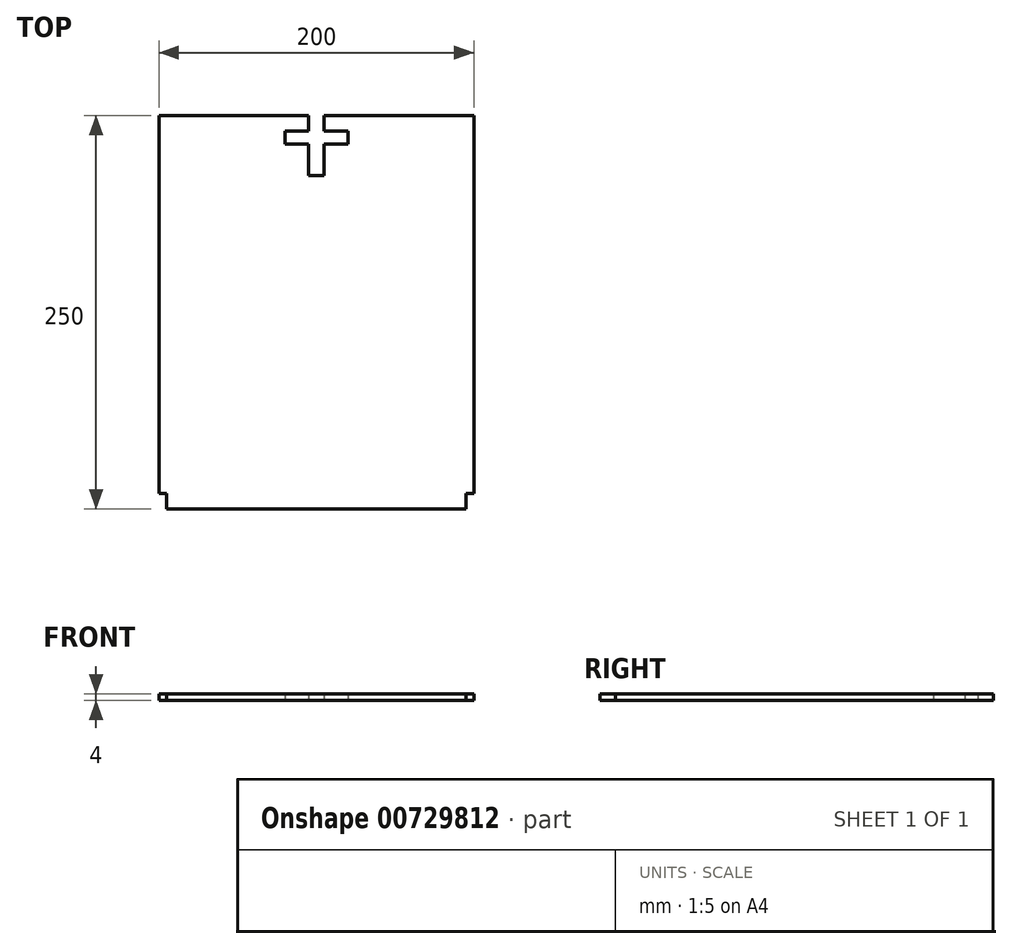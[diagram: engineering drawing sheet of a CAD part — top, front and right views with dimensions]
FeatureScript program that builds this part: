
annotation { "Feature Type Name" : "Feature", "Feature Type Description" : "" }
export const myFeature = defineFeature(function(context is Context, id is Id, definition is map)
    precondition{}
    {
        {
            var Q0;
            Q0=qCreatedBy(makeId("Top.planeOp"),FACE);
            var sketch = newSketch(context, id + "F0", { "sketchPlane" : qUnion([Q0])});
            skLineSegment(sketch, "E0.bottom", {"start": v(20, -10) * mm, "end": v(5, -10) * mm});
            skLineSegment(sketch, "E0.left", {"start": v(20, -10) * mm, "end": v(20, -18) * mm});
            skLineSegment(sketch, "E0.right", {"start": v(-20, -10) * mm, "end": v(-20, -18) * mm});
            skPoint(sketch, "E0.middle", {"position": v(0, 0) * mm});
            skLineSegment(sketch, "E1.top", {"start": v(-100, 0) * mm, "end": v(-5, 0) * mm});
            skLineSegment(sketch, "E1.left", {"start": v(-100, -240) * mm, "end": v(-100, 0) * mm});
            skLineSegment(sketch, "E1.right", {"start": v(100, -240) * mm, "end": v(100, 0) * mm});
            skLineSegment(sketch, "E2", {"start": v(20, -18) * mm, "end": v(5, -18) * mm});
            skLineSegment(sketch, "E3", {"start": v(5, -18) * mm, "end": v(5, -38) * mm});
            skLineSegment(sketch, "E4", {"start": v(-20, -18) * mm, "end": v(-5, -18) * mm});
            skLineSegment(sketch, "E5", {"start": v(-5, -18) * mm, "end": v(-5, -38) * mm});
            skLineSegment(sketch, "E6", {"start": v(0, 0) * mm, "end": v(0, -10) * mm, "construction": true});
            skLineSegment(sketch, "E7", {"start": v(95, -250) * mm, "end": v(-95, -250) * mm});
            skLineSegment(sketch, "E8", {"start": v(0, -38) * mm, "end": v(0, -250) * mm, "construction": true});
            skLineSegment(sketch, "E9", {"start": v(-100, -240) * mm, "end": v(-95, -240) * mm});
            skLineSegment(sketch, "E10", {"start": v(-95, -240) * mm, "end": v(-95, -250) * mm});
            skLineSegment(sketch, "E11", {"start": v(100, -240) * mm, "end": v(95, -240) * mm});
            skLineSegment(sketch, "E12", {"start": v(95, -240) * mm, "end": v(95, -250) * mm});
            skLineSegment(sketch, "E13", {"start": v(5, 0) * mm, "end": v(100, 0) * mm});
            skLineSegment(sketch, "E14", {"start": v(5, -10) * mm, "end": v(0, -10) * mm, "construction": true});
            skLineSegment(sketch, "E15", {"start": v(-5, 0) * mm, "end": v(5, 0) * mm, "construction": true});
            skLineSegment(sketch, "E16", {"start": v(-5, -10) * mm, "end": v(-20, -10) * mm});
            skLineSegment(sketch, "E17", {"start": v(5, 0) * mm, "end": v(5, -10) * mm});
            skLineSegment(sketch, "E18", {"start": v(-5, -10) * mm, "end": v(-5, 0) * mm});
            skLineSegment(sketch, "E19", {"start": v(0, -10) * mm, "end": v(-5, -10) * mm, "construction": true});
            skLineSegment(sketch, "E20", {"start": v(-5, -38) * mm, "end": v(5, -38) * mm});
            skSolve(sketch);
        }
        {
            var Q0;
            Q0=qSketchRegion(id+"F0",true);
            extrude(context, id + "F1", {"entities" : qUnion([Q0]), "depth" : 4 * mm, "offsetDistance" : 25 * mm});
        }
    });
